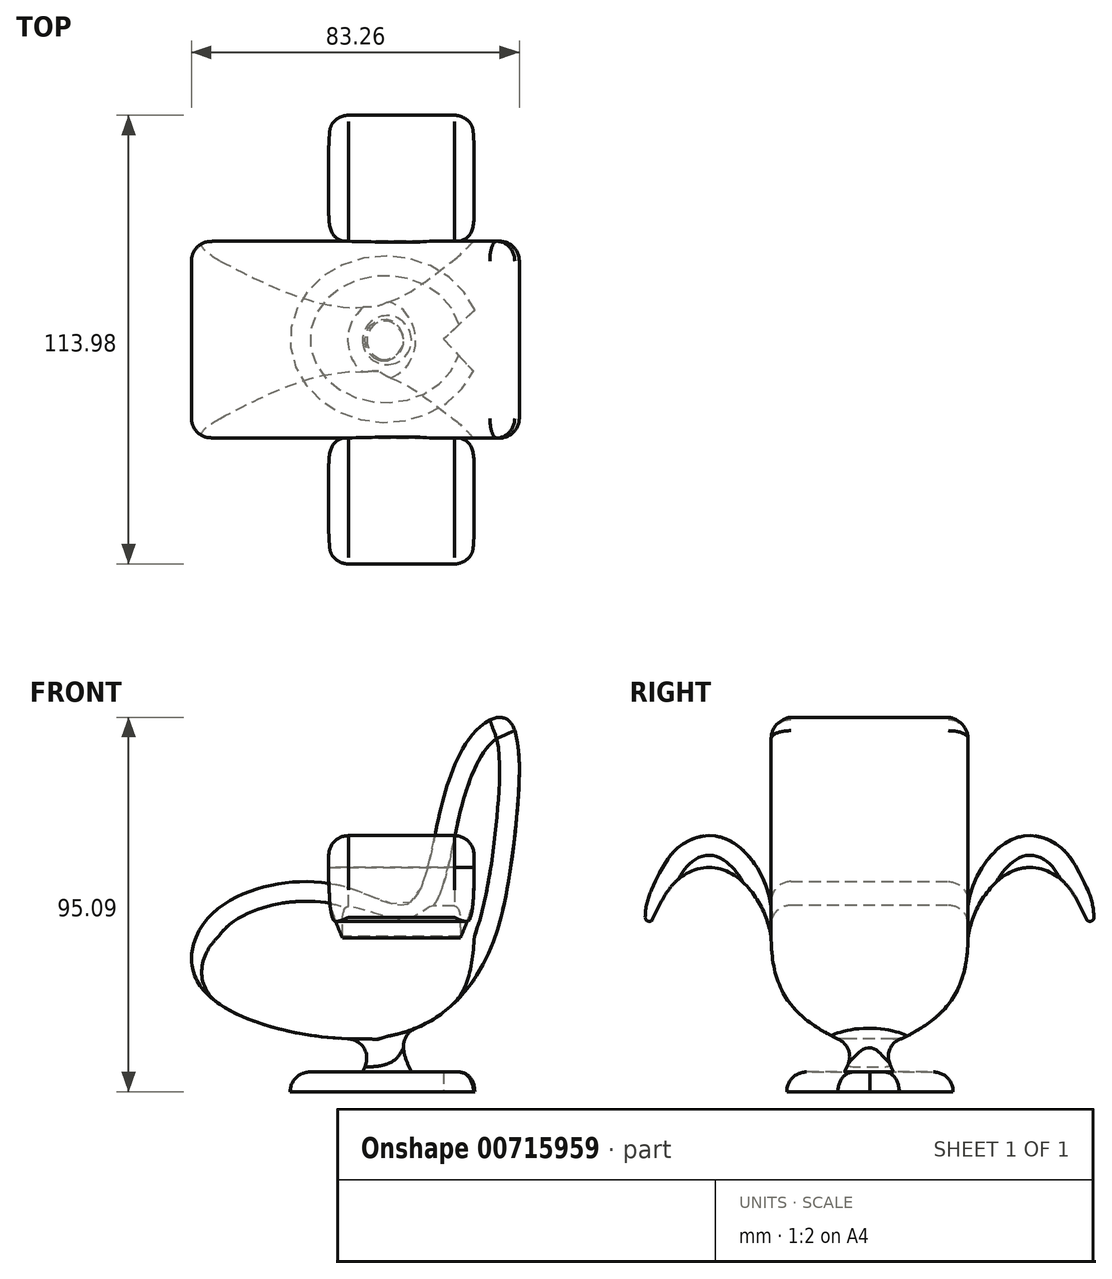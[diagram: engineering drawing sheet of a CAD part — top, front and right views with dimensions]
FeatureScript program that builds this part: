
annotation { "Feature Type Name" : "Feature", "Feature Type Description" : "" }
export const myFeature = defineFeature(function(context is Context, id is Id, definition is map)
    precondition{}
    {
        {
            var Q0;
            Q0=qCreatedBy(makeId("Front.planeOp"),FACE);
            var sketch = newSketch(context, id + "F0", { "sketchPlane" : qUnion([Q0])});
            skFitSpline(sketch, "E0", {"points": [v(2.37, -9.2) * mm, v(10.32, 14.23) * mm, v(20.57, 35.77) * mm, v(27.89, 37.03) * mm, v(29.14, 6.9) * mm, v(21.82, -23.63) * mm, v(8.23, -38.9) * mm, v(-16.25, -43.5) * mm, v(-50.76, -30.11) * mm, v(-47.41, -11.7) * mm, v(-15.62, -4.6) * mm, v(2.37, -9.2) * mm]});
            skSolve(sketch);
        }
        {
            var Q0;
            Q0 = qSketchRegion(id + "F0", true);
            extrude(context, id + "F1", {"entities" : qUnion([Q0]), "depth" : 50 * mm, "offsetDistance" : 25 * mm});
        }
        {
            var Q0;
            Q0=qCreatedBy(makeId("Right.planeOp"),FACE);
            var sketch = newSketch(context, id + "F2", { "sketchPlane" : qUnion([Q0])});
            skFitSpline(sketch, "E1", {"points": [v(-49.78, -12.45) * mm, v(-57.1, 4.7) * mm, v(-65.89, 8.47) * mm, v(-74.26, 4.91) * mm, v(-82, -8.68) * mm], "startDerivative": vector(-0.26, 71.4) * mm, "endDerivative": vector(-31.79, -66.51) * mm});
            skSolve(sketch);
        }
        {
            var Q0;
            Q0=qCreatedBy(makeId("Front.planeOp"),FACE);
            cPlane(context, id + "F3", {"entities" : qUnion([Q0]), "cplaneType" : CPlaneType.OFFSET, "offset" : 50 * mm, "width" : 150 * mm, "height" : 150 * mm});
        }
        {
            var Q0;
            Q0=qCreatedBy(id+"F3.planeOp",FACE);
            var sketch = newSketch(context, id + "F4", { "sketchPlane" : qUnion([Q0])});
            skLineSegment(sketch, "E2.bottom", {"start": v(-18, -9.92) * mm, "end": v(18.94, -9.92) * mm});
            skLineSegment(sketch, "E2.top", {"start": v(-18, -18.03) * mm, "end": v(18.94, -18.03) * mm});
            skLineSegment(sketch, "E2.left", {"start": v(-18, -9.92) * mm, "end": v(-18, -18.03) * mm});
            skLineSegment(sketch, "E2.right", {"start": v(18.94, -9.92) * mm, "end": v(18.94, -18.03) * mm});
            skSolve(sketch);
        }
        {
            var Q0;
            Q0 = qSketchRegion(id + "F4", true);
            var Q1;
            Q1 = qConstructionFilter(qBodyType(qCreatedBy(id + "F2" ,EDGE), BodyType.WIRE), ConstructionObject.NO);
            sweep(context, id + "F5", {"profiles" : qUnion([Q0]), "path" : qUnion([Q1]), "keepProfileOrientation" : true});
        }
        {
            var Q0;
            Q0=qCreatedBy(makeId("Front.planeOp"),FACE);
            cPlane(context, id + "F6", {"entities" : qUnion([Q0]), "cplaneType" : CPlaneType.OFFSET, "offset" : 25 * mm, "width" : 150 * mm, "height" : 150 * mm});
        }
        {
            var Q0;
            Q0=makeQuery(id+"F5.opSweep","SWEPT_BODY",BODY,{"disambiguationData":[OSD([sQuery(id+"F2.wireOp",EDGE,"E1"),sQuery(id+"F4.wireOp",EDGE,"E2.bottom"),sQuery(id+"F4.wireOp",EDGE,"E2.top"),sQuery(id+"F4.wireOp",EDGE,"E2.left"),sQuery(id+"F4.wireOp",EDGE,"E2.right")])]});
            var Q1;
            Q1=qCreatedBy(id+"F6.planeOp",FACE);
            mirror(context, id + "F7", {"operationType" : NewBodyOperationType.ADD, "entities" : qUnion([Q0]), "mirrorPlane" : qUnion([Q1])});
        }
        {
            var Q0;
            Q0=makeQuery(id+"F7.opPattern","COPY",EDGE,{"derivedFrom":makeQuery(id+"F5.opSweep","CAP_EDGE",EDGE,{"disambiguationData":[OSD([sQuery(id+"F2.wireOp",VERTEX,"E1.end"),sQuery(id+"F4.wireOp",EDGE,"E2.top")])],"isStart":false}),"instanceName":"1"});
            var Q1;
            Q1=makeQuery(id+"F5.opSweep","CAP_EDGE",EDGE,{"disambiguationData":[OSD([sQuery(id+"F2.wireOp",VERTEX,"E1.end"),sQuery(id+"F4.wireOp",EDGE,"E2.top")])],"isStart":false});
            fillet(context, id + "F8", {"entities" : qUnion([Q0, Q1]), "radius" : 1 * mm, "tangentPropagation" : true, "allowEdgeOverflow" : false});
        }
        {
            var Q0;
            Q0=makeQuery(id+"F7.opPattern","COPY",EDGE,{"derivedFrom":makeQuery(id+"F5.opSweep","CAP_EDGE",EDGE,{"disambiguationData":[OSD([sQuery(id+"F2.wireOp",VERTEX,"E1.end"),sQuery(id+"F4.wireOp",EDGE,"E2.bottom")])],"isStart":false}),"instanceName":"1"});
            var Q1;
            Q1=makeQuery(id+"F5.opSweep","CAP_EDGE",EDGE,{"disambiguationData":[OSD([sQuery(id+"F2.wireOp",VERTEX,"E1.end"),sQuery(id+"F4.wireOp",EDGE,"E2.bottom")])],"isStart":false});
            fillet(context, id + "F9", {"entities" : qUnion([Q0, Q1]), "radius" : 17 * mm, "tangentPropagation" : true, "allowEdgeOverflow" : false});
        }
        {
            var Q0;
            Q0=qCreatedBy(makeId("Right.planeOp"),FACE);
            cPlane(context, id + "F10", {"entities" : qUnion([Q0]), "cplaneType" : CPlaneType.OFFSET, "offset" : 3.2 * mm, "oppositeDirection" : true, "width" : 150 * mm, "height" : 150 * mm});
        }
        {
            var Q0;
            Q0=qCreatedBy(id+"F10.planeOp",FACE);
            var sketch = newSketch(context, id + "F11", { "sketchPlane" : qUnion([Q0])});
            skFitSpline(sketch, "E3", {"points": [v(-31.34, -36.23) * mm, v(-29.65, -47.88) * mm, v(-32.1, -55.03) * mm, v(-25.14, -55.03) * mm], "startDerivative": vector(10.27, -30.28) * mm, "endDerivative": vector(32.02, 5.54) * mm});
            skLineSegment(sketch, "E4", {"start": v(-25.14, -55.03) * mm, "end": v(-25.14, -35.48) * mm});
            skLineSegment(sketch, "E5", {"start": v(-25.14, -35.48) * mm, "end": v(-31.34, -36.23) * mm});
            skSolve(sketch);
        }
        {
            var Q0;
            Q0=makeQuery(id+"F11.imprint","IMPRINT",FACE,{"disambiguationData":[TD([[makeQuery(id+"F11.imprint","IMPRINT",EDGE,{"derivedFrom":sQuery(id+"F11.wireOp",EDGE,"E3")}),1.0]])]});
            var Q1;
            Q1=sQuery(id+"F11.wireOp",EDGE,"E4");
            revolve(context, id + "F12", {"operationType" : NewBodyOperationType.ADD, "surfaceOperationType" : NewSurfaceOperationType.NEW, "entities" : qUnion([Q0]), "axis" : qUnion([Q1]), "revolveType" : RevolveType.FULL});
        }
        {
            var Q0;
            Q0=qCreatedBy(makeId("Top.planeOp"),FACE);
            cPlane(context, id + "F13", {"entities" : qUnion([Q0]), "cplaneType" : CPlaneType.OFFSET, "offset" : 57.1 * mm, "oppositeDirection" : true, "width" : 150 * mm, "height" : 150 * mm});
        }
        {
            var Q0;
            Q0=qCreatedBy(id+"F13.planeOp",FACE);
            var sketch = newSketch(context, id + "F14", { "sketchPlane" : qUnion([Q0])});
            skEllipticalArc(sketch, "E6", {});
            skLineSegment(sketch, "E7", {"start": v(19.1, -17.45) * mm, "end": v(11.16, -24.9) * mm});
            skLineSegment(sketch, "E8", {"start": v(11.16, -24.9) * mm, "end": v(18.79, -33.04) * mm});
            const initialGuessF14  = {"E6": [-0.0035683729220181704, -0.02489684335887432, 1, 0, 0.024228331262608788, 0.021141451869788472, 0.3597500603199456, 5.887563689546112]};
            skSetInitialGuess(sketch, initialGuessF14);
            skSolve(sketch);
        }
        {
            var Q0;
            Q0 = qSketchRegion(id + "F14", true);
            extrude(context, id + "F15", {"entities" : qUnion([Q0]), "operationType" : NewBodyOperationType.ADD, "depth" : 5 * mm, "offsetDistance" : 25 * mm});
        }
        {
            var Q0;
            Q0=makeQuery(id+"F15.opExtrude","CAP_EDGE",EDGE,{"disambiguationData":[OSD([sQuery(id+"F14.wireOp",EDGE,"E6")])],"isStart":false});
            fillet(context, id + "F16", {"entities" : qUnion([Q0]), "radius" : 5 * mm, "tangentPropagation" : true, "allowEdgeOverflow" : false});
        }
        {
            var Q0;
            Q0=makeQuery(id+"F5.opSweep","SWEPT_EDGE",EDGE,{"disambiguationData":[OSD([sQuery(id+"F2.wireOp",EDGE,"E1"),sQuery(id+"F4.wireOp",EDGE,"E2.bottom"),sQuery(id+"F4.wireOp",EDGE,"E2.right")])]});
            var Q1;
            Q1=makeQuery(id+"F5.opSweep","SWEPT_EDGE",EDGE,{"disambiguationData":[OSD([sQuery(id+"F2.wireOp",EDGE,"E1"),sQuery(id+"F4.wireOp",EDGE,"E2.bottom"),sQuery(id+"F4.wireOp",EDGE,"E2.left")])]});
            var Q2;
            Q2=makeQuery(id+"F7.opPattern","COPY",EDGE,{"derivedFrom":makeQuery(id+"F5.opSweep","SWEPT_EDGE",EDGE,{"disambiguationData":[OSD([sQuery(id+"F2.wireOp",EDGE,"E1"),sQuery(id+"F4.wireOp",EDGE,"E2.bottom"),sQuery(id+"F4.wireOp",EDGE,"E2.right")])]}),"instanceName":"1"});
            var Q3;
            Q3=makeQuery(id+"F7.opPattern","COPY",EDGE,{"derivedFrom":makeQuery(id+"F5.opSweep","SWEPT_EDGE",EDGE,{"disambiguationData":[OSD([sQuery(id+"F2.wireOp",EDGE,"E1"),sQuery(id+"F4.wireOp",EDGE,"E2.bottom"),sQuery(id+"F4.wireOp",EDGE,"E2.left")])]}),"instanceName":"1"});
            fillet(context, id + "F17", {"entities" : qUnion([Q0, Q1, Q2, Q3]), "radius" : 5 * mm, "tangentPropagation" : true, "allowEdgeOverflow" : false});
        }
        {
            var Q0;
            Q0=makeQuery(id+"F1.opExtrude","CAP_EDGE",EDGE,{"disambiguationData":[OSD([sQuery(id+"F0.wireOp",EDGE,"E0")])],"isStart":false});
            var Q1;
            Q1=makeQuery(id+"F1.opExtrude","SWEPT_FACE",FACE,{"disambiguationData":[OSD([sQuery(id+"F0.wireOp",EDGE,"E0")])]});
            fillet(context, id + "F18", {"entities" : qUnion([Q0, Q1]), "radius" : 5 * mm, "tangentPropagation" : true, "allowEdgeOverflow" : false});
        }
        {
            var Q0;
            Q0=qCreatedBy(makeId("Right.planeOp"),FACE);
            cPlane(context, id + "F19", {"entities" : qUnion([Q0]), "cplaneType" : CPlaneType.OFFSET, "offset" : 53.7 * mm, "oppositeDirection" : true, "width" : 150 * mm, "height" : 150 * mm});
        }
        {
            var Q0;
            Q0=qCreatedBy(id+"F19.planeOp",FACE);
            var sketch = newSketch(context, id + "F20", { "sketchPlane" : qUnion([Q0])});
            skFitSpline(sketch, "E9", {"points": [v(0, -17.64) * mm, v(-17, -43.76) * mm], "startDerivative": vector(0, -45.1) * mm, "endDerivative": vector(-31.58, -15.79) * mm});
            skLineSegment(sketch, "E10", {"start": v(0, -17.64) * mm, "end": v(0, -43.95) * mm});
            skLineSegment(sketch, "E11", {"start": v(0, -43.95) * mm, "end": v(-17, -43.76) * mm});
            skFitSpline(sketch, "E12.MirrorCS", {"points": [v(-50, -17.64) * mm, v(-33, -43.76) * mm], "startDerivative": vector(0, -45.1) * mm, "endDerivative": vector(31.58, -15.79) * mm});
            skLineSegment(sketch, "E13.MirrorCS", {"start": v(-50, -43.95) * mm, "end": v(-33, -43.76) * mm});
            skLineSegment(sketch, "E14.MirrorCS", {"start": v(-50, -17.64) * mm, "end": v(-50, -43.95) * mm});
            skSolve(sketch);
        }
        {
            var Q0;
            Q0 = qSketchRegion(id + "F20", true);
            extrude(context, id + "F21", {"entities" : qUnion([Q0]), "operationType" : NewBodyOperationType.REMOVE, "depth" : 80 * mm, "offsetDistance" : 25 * mm});
        }
    });
